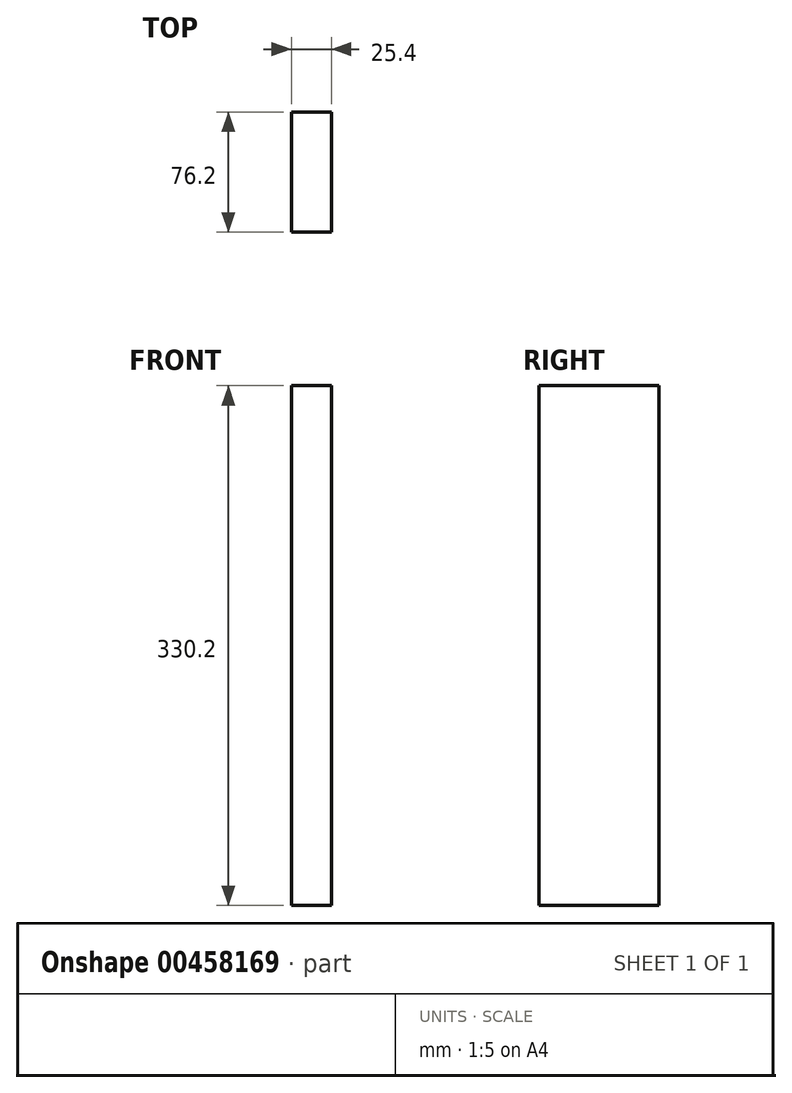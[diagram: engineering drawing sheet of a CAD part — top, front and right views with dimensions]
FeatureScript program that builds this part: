
annotation { "Feature Type Name" : "Feature", "Feature Type Description" : "" }
export const myFeature = defineFeature(function(context is Context, id is Id, definition is map)
    precondition{}
    {
        {
            var Q0;
            Q0=qCreatedBy(makeId("Top.planeOp"),FACE);
            var sketch = newSketch(context, id + "F0", { "sketchPlane" : qUnion([Q0])});
            skLineSegment(sketch, "E0.bottom", {"start": v(-13.26, 40) * mm, "end": v(12.14, 40) * mm});
            skLineSegment(sketch, "E0.top", {"start": v(-13.26, -36.2) * mm, "end": v(12.14, -36.2) * mm});
            skLineSegment(sketch, "E0.left", {"start": v(-13.26, 40) * mm, "end": v(-13.26, -36.2) * mm});
            skLineSegment(sketch, "E0.right", {"start": v(12.14, 40) * mm, "end": v(12.14, -36.2) * mm});
            skSolve(sketch);
        }
        {
            var Q0;
            Q0 = qSketchRegion(id + "F0", true);
            extrude(context, id + "F1", {"entities" : qUnion([Q0]), "depth" : 330.2 * mm});
        }
    });
